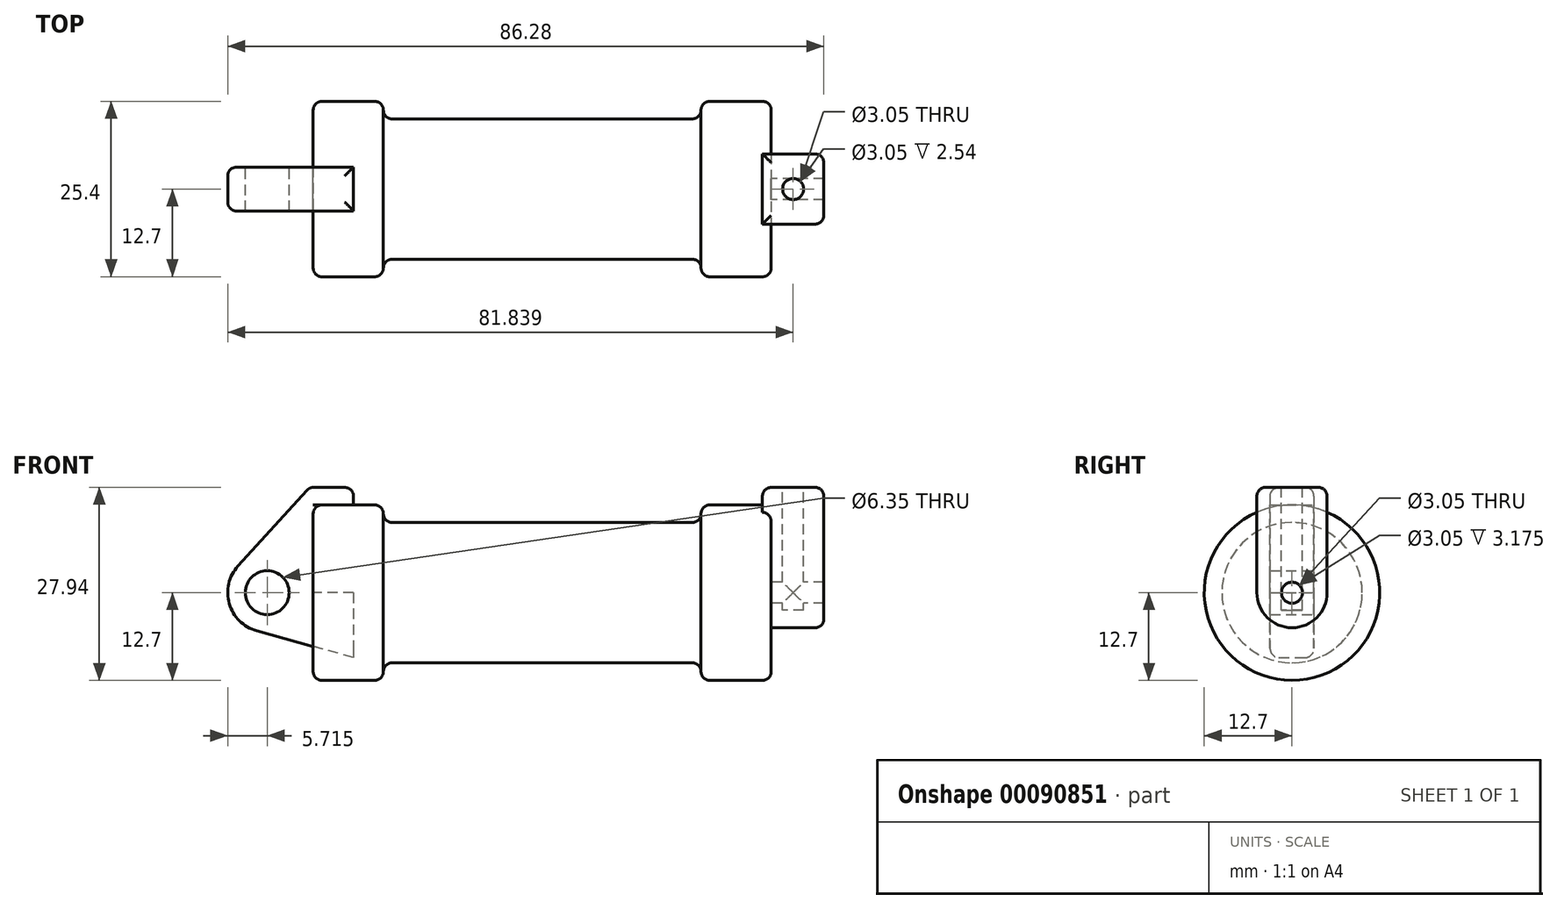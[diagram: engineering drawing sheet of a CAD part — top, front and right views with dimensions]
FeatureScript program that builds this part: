
annotation { "Feature Type Name" : "Feature", "Feature Type Description" : "" }
export const myFeature = defineFeature(function(context is Context, id is Id, definition is map)
    precondition{}
    {
        {
            var Q0;
            Q0=qCreatedBy(makeId("Front.planeOp"),FACE);
            var sketch = newSketch(context, id + "F0", { "sketchPlane" : qUnion([Q0])});
            skLineSegment(sketch, "E0", {"start": v(0, 0) * mm, "end": v(0, 12.7) * mm});
            skLineSegment(sketch, "E1", {"start": v(0, 12.7) * mm, "end": v(10.16, 12.7) * mm});
            skLineSegment(sketch, "E2", {"start": v(10.16, 12.7) * mm, "end": v(10.16, 10.16) * mm});
            skLineSegment(sketch, "E3", {"start": v(10.16, 10.16) * mm, "end": v(56.13, 10.16) * mm});
            skLineSegment(sketch, "E4", {"start": v(56.13, 10.16) * mm, "end": v(56.13, 12.7) * mm});
            skLineSegment(sketch, "E5", {"start": v(56.13, 12.7) * mm, "end": v(66.3, 12.7) * mm});
            skLineSegment(sketch, "E6", {"start": v(66.3, 12.7) * mm, "end": v(66.3, 0) * mm});
            skLineSegment(sketch, "E7", {"start": v(66.3, 0) * mm, "end": v(0, 0) * mm});
            skLineSegment(sketch, "E8", {"start": v(5.84, 15.24) * mm, "end": v(-0.5, 15.24) * mm});
            skLineSegment(sketch, "E9", {"start": v(-0.5, 15.24) * mm, "end": v(-10.88, 3.85) * mm});
            skLineSegment(sketch, "E10", {"start": v(0, 0) * mm, "end": v(-6.65, 0) * mm});
            skCircle(sketch, "E11", {"center": v(-6.65, 0) * mm, "radius": 5.72 * mm});
            skCircle(sketch, "E12", {"center": v(-6.65, 0) * mm, "radius": 3.18 * mm});
            skLineSegment(sketch, "E13", {"start": v(5.84, 15.24) * mm, "end": v(5.84, -9.4) * mm});
            skLineSegment(sketch, "E14", {"start": v(5.84, -9.4) * mm, "end": v(-8.18, -5.5) * mm});
            skSolve(sketch);
        }
        {
            var Q0;
            {var subQ0=sQuery(id+"F0.wireOp",EDGE,"E0");Q0=makeQuery(id+"F0.imprint","IMPRINT",FACE,{"disambiguationData":[TD([[makeQuery(id+"F0.imprint","IMPRINT",EDGE,{"derivedFrom":subQ0}),-1.0]])]});}
            var Q1;
            {var subQ0=sQuery(id+"F0.wireOp",EDGE,"E2");Q1=makeQuery(id+"F0.imprint","IMPRINT",FACE,{"disambiguationData":[TD([[makeQuery(id+"F0.imprint","IMPRINT",EDGE,{"derivedFrom":subQ0}),-1.0]])]});}
            var Q2;
            Q2=sQuery(id+"F0.wireOp",EDGE,"E7");
            revolve(context, id + "F1", {"entities" : qUnion([Q0, Q1]), "axis" : qUnion([Q2]), "revolveType" : RevolveType.FULL});
        }
        {
            var Q0;
            Q0=makeQuery(id+"F1.opRevolve","SWEPT_FACE",FACE,{"disambiguationData":[OSD([sQuery(id+"F0.wireOp",EDGE,"E6")])]});
            var sketch = newSketch(context, id + "F2", { "sketchPlane" : qUnion([Q0])});
            skCircle(sketch, "E15", {"center": v(0, 0) * mm, "radius": 1.52 * mm});
            skCircle(sketch, "E16", {"center": v(0, 0) * mm, "radius": 5.08 * mm});
            skLineSegment(sketch, "E17", {"start": v(-5.08, 15.24) * mm, "end": v(5.08, 15.24) * mm});
            skLineSegment(sketch, "E18", {"start": v(-5.08, 15.24) * mm, "end": v(-5.08, 0) * mm});
            skLineSegment(sketch, "E19", {"start": v(5.08, 15.24) * mm, "end": v(5.08, 0) * mm});
            skSolve(sketch);
        }
        {
            var Q0;
            {var subQ0=sQuery(id+"F2.wireOp",EDGE,"E17");Q0=makeQuery(id+"F2.imprint","IMPRINT",FACE,{"disambiguationData":[TD([[makeQuery(id+"F2.imprint","IMPRINT",EDGE,{"derivedFrom":subQ0}),-1.0]])]});}
            var Q1;
            {var subQ0=sQuery(id+"F2.wireOp",EDGE,"E18");var subQ1=sQuery(id+"F2.wireOp",EDGE,"E16");var subQ2=makeQuery(id+"F2.imprint","INTERSECT",VERTEX,{"derivedFrom":[subQ1,subQ0]});Q1=makeQuery(id+"F2.imprint","IMPRINT",FACE,{"disambiguationData":[TD([[makeQuery(id+"F2.imprint","IMPRINT",EDGE,{"disambiguationData":[TD([[subQ2,1.0]])],"derivedFrom":subQ1}),-1.0]])]});}
            var Q2;
            Q2=makeQuery(id+"F2.imprint","IMPRINT",FACE,{"disambiguationData":[TD([[makeQuery(id+"F2.imprint","IMPRINT",EDGE,{"derivedFrom":sQuery(id+"F2.wireOp",EDGE,"E15")}),-1.0]])]});
            extrude(context, id + "F3", {"entities" : qUnion([Q0, Q1, Q2]), "operationType" : NewBodyOperationType.ADD, "depth" : 7.62 * mm, "hasSecondDirection" : true, "secondDirectionOppositeDirection" : true, "secondDirectionDepth" : 1.27 * mm});
        }
        {
            var Q0;
            Q0=makeQuery(id+"F3.opExtrude","SWEPT_FACE",FACE,{"disambiguationData":[OSD([sQuery(id+"F2.wireOp",EDGE,"E17")])]});
            var sketch = newSketch(context, id + "F4", { "sketchPlane" : qUnion([Q0])});
            skCircle(sketch, "E20", {"center": v(69.47, 0) * mm, "radius": 1.52 * mm});
            skSolve(sketch);
        }
        {
            var Q0;
            Q0=makeQuery(id+"F4.imprint","IMPRINT",FACE,{"disambiguationData":[TD([[makeQuery(id+"F4.imprint","IMPRINT",EDGE,{"derivedFrom":sQuery(id+"F4.wireOp",EDGE,"E20")}),1.0]])]});
            var Q1;
            Q1=sQuery(id+"F4.wireOp",EDGE,"E20");
            extrude(context, id + "F5", {"entities" : qUnion([Q0]), "operationType" : NewBodyOperationType.REMOVE, "surfaceEntities" : qUnion([Q1]), "oppositeDirection" : true, "depth" : 17.78 * mm});
        }
        {
            var Q0;
            {var subQ3=sQuery(id+"F0.wireOp",EDGE,"E0");Q0=makeQuery(id+"F0.imprint","IMPRINT",FACE,{"disambiguationData":[TD([[makeQuery(id+"F0.imprint","IMPRINT",EDGE,{"derivedFrom":subQ3}),1.0]])]});}
            var Q1;
            {var subQ4=sQuery(id+"F0.wireOp",EDGE,"E12");Q1=makeQuery(id+"F0.imprint","IMPRINT",FACE,{"disambiguationData":[TD([[makeQuery(id+"F0.imprint","IMPRINT",EDGE,{"derivedFrom":subQ4}),-1.0]])]});}
            var Q2;
            {var subQ0=sQuery(id+"F0.wireOp",EDGE,"E14");Q2=makeQuery(id+"F0.imprint","IMPRINT",FACE,{"disambiguationData":[TD([[makeQuery(id+"F0.imprint","IMPRINT",EDGE,{"derivedFrom":subQ0}),-1.0]])]});}
            extrude(context, id + "F6", {"entities" : qUnion([Q0, Q1, Q2]), "endBound" : BoundingType.SYMMETRIC, "depth" : 6.35 * mm});
        }
        {
            var Q0;
            Q0=makeQuery(id+"F1.opRevolve","SWEPT_FACE",FACE,{"disambiguationData":[OSD([sQuery(id+"F0.wireOp",EDGE,"E3")])]});
            fillet(context, id + "F7", {"entities" : qUnion([Q0]), "radius" : 1.27 * mm, "tangentPropagation" : true, "allowEdgeOverflow" : false});
        }
        {
            var Q0;
            Q0=makeQuery(id+"F6.opExtrude","SWEPT_FACE",FACE,{"disambiguationData":[OSD([sQuery(id+"F0.wireOp",EDGE,"E8")])]});
            var Q1;
            Q1=makeQuery(id+"F6.opExtrude","CAP_EDGE",EDGE,{"disambiguationData":[OSD([sQuery(id+"F0.wireOp",EDGE,"E9")])],"isStart":true});
            var Q2;
            Q2=makeQuery(id+"F6.opExtrude","CAP_EDGE",EDGE,{"disambiguationData":[OSD([sQuery(id+"F0.wireOp",EDGE,"E11")])],"isStart":true});
            var Q3;
            Q3=makeQuery(id+"F6.opExtrude","CAP_EDGE",EDGE,{"disambiguationData":[OSD([sQuery(id+"F0.wireOp",EDGE,"E14")])],"isStart":true});
            var Q4;
            Q4=makeQuery(id+"F6.opExtrude","CAP_EDGE",EDGE,{"disambiguationData":[OSD([sQuery(id+"F0.wireOp",EDGE,"E14")])],"isStart":false});
            var Q5;
            Q5=makeQuery(id+"F6.opExtrude","SWEPT_FACE",FACE,{"disambiguationData":[OSD([sQuery(id+"F0.wireOp",EDGE,"E11")])]});
            var Q6;
            Q6=makeQuery(id+"F6.opExtrude","SWEPT_FACE",FACE,{"disambiguationData":[OSD([sQuery(id+"F0.wireOp",EDGE,"E9")])]});
            var Q7;
            Q7=makeQuery(id+"F6.opExtrude","CAP_EDGE",EDGE,{"disambiguationData":[OSD([sQuery(id+"F0.wireOp",EDGE,"E9")])],"isStart":false});
            var Q8;
            Q8=makeQuery(id+"F6.opExtrude","CAP_EDGE",EDGE,{"disambiguationData":[OSD([sQuery(id+"F0.wireOp",EDGE,"E11")])],"isStart":false});
            fillet(context, id + "F8", {"entities" : qUnion([Q0, Q1, Q2, Q3, Q4, Q5, Q6, Q7, Q8]), "radius" : 1.27 * mm, "allowEdgeOverflow" : false});
        }
        {
            var Q0;
            Q0=makeQuery(id+"F1.opRevolve","SWEPT_EDGE",EDGE,{"disambiguationData":[OSD([sQuery(id+"F0.wireOp",EDGE,"E4"),sQuery(id+"F0.wireOp",EDGE,"E5")])]});
            var Q1;
            Q1=makeQuery(id+"F1.opRevolve","SWEPT_FACE",FACE,{"disambiguationData":[OSD([sQuery(id+"F0.wireOp",EDGE,"E1")])]});
            var Q2;
            Q2=makeQuery(id+"F1.opRevolve","SWEPT_EDGE",EDGE,{"disambiguationData":[OSD([sQuery(id+"F0.wireOp",EDGE,"E5"),sQuery(id+"F0.wireOp",EDGE,"E6")])]});
            var Q3;
            Q3=makeQuery(id+"F3.opExtrude","CAP_EDGE",EDGE,{"disambiguationData":[OSD([sQuery(id+"F2.wireOp",EDGE,"E19")])],"isStart":false});
            var Q4;
            Q4=makeQuery(id+"F3.opExtrude","SWEPT_EDGE",EDGE,{"disambiguationData":[OSD([sQuery(id+"F2.wireOp",EDGE,"E17"),sQuery(id+"F2.wireOp",EDGE,"E19")])]});
            var Q5;
            Q5=makeQuery(id+"F3.opExtrude","SWEPT_EDGE",EDGE,{"disambiguationData":[OSD([sQuery(id+"F2.wireOp",EDGE,"E17"),sQuery(id+"F2.wireOp",EDGE,"E18")])]});
            var Q6;
            Q6=makeQuery(id+"F3.opExtrude","CAP_EDGE",EDGE,{"disambiguationData":[OSD([sQuery(id+"F2.wireOp",EDGE,"E17")])],"isStart":false});
            var Q7;
            Q7=makeQuery(id+"F3.opExtrude","CAP_EDGE",EDGE,{"disambiguationData":[OSD([sQuery(id+"F2.wireOp",EDGE,"E17")])],"isStart":true});
            fillet(context, id + "F9", {"entities" : qUnion([Q0, Q1, Q2, Q3, Q4, Q5, Q6, Q7]), "radius" : 1.27 * mm, "tangentPropagation" : true, "allowEdgeOverflow" : false});
        }
    });
